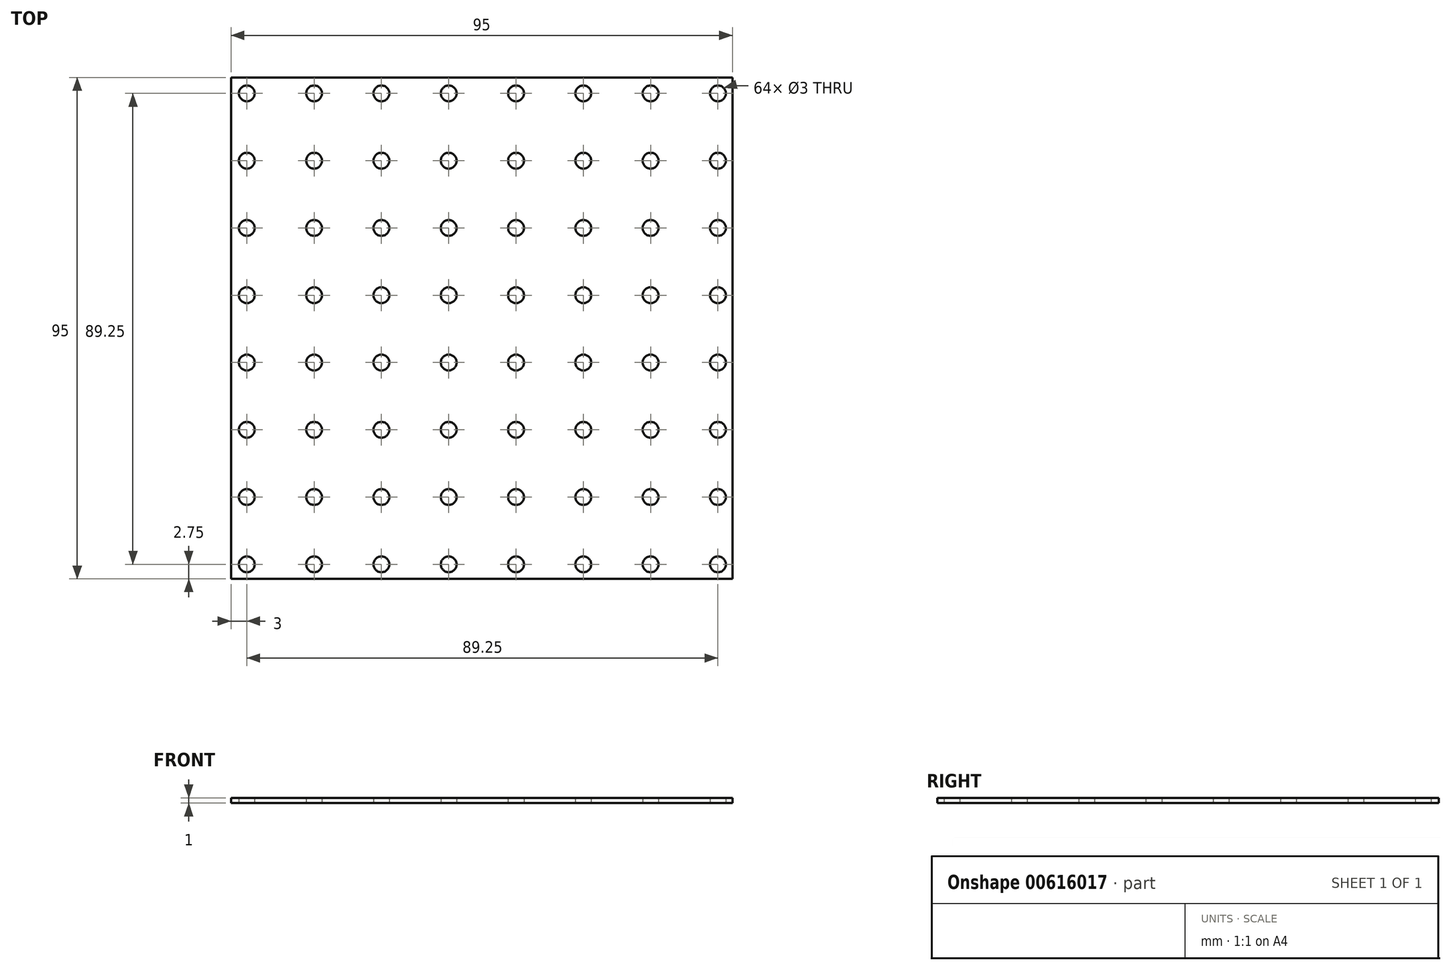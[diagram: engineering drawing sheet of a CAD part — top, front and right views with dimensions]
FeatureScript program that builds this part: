
annotation { "Feature Type Name" : "Feature", "Feature Type Description" : "" }
export const myFeature = defineFeature(function(context is Context, id is Id, definition is map)
    precondition{}
    {
        {
            var Q0;
            Q0=qCreatedBy(makeId("Top.planeOp"),FACE);
            var sketch = newSketch(context, id + "F0", { "sketchPlane" : qUnion([Q0])});
            skLineSegment(sketch, "E0.bottom", {"start": v(47.5, -47.5) * mm, "end": v(-47.5, -47.5) * mm});
            skLineSegment(sketch, "E0.top", {"start": v(47.5, 47.5) * mm, "end": v(-47.5, 47.5) * mm});
            skLineSegment(sketch, "E0.left", {"start": v(47.5, -47.5) * mm, "end": v(47.5, 47.5) * mm});
            skLineSegment(sketch, "E0.right", {"start": v(-47.5, -47.5) * mm, "end": v(-47.5, 47.5) * mm});
            skPoint(sketch, "E0.middle", {"position": v(0, 0) * mm});
            skCircle(sketch, "E1", {"center": v(-44.5, 44.5) * mm, "radius": 1.5 * mm});
            skCircle(sketch, "E2.0.1.0", {"center": v(-44.5, 31.75) * mm, "radius": 1.5 * mm});
            skCircle(sketch, "E2.0.2.0", {"center": v(-44.5, 19) * mm, "radius": 1.5 * mm});
            skCircle(sketch, "E2.0.3.0", {"center": v(-44.5, 6.25) * mm, "radius": 1.5 * mm});
            skCircle(sketch, "E2.0.4.0", {"center": v(-44.5, -6.5) * mm, "radius": 1.5 * mm});
            skCircle(sketch, "E2.0.5.0", {"center": v(-44.5, -19.25) * mm, "radius": 1.5 * mm});
            skCircle(sketch, "E2.0.6.0", {"center": v(-44.5, -32) * mm, "radius": 1.5 * mm});
            skCircle(sketch, "E2.0.7.0", {"center": v(-44.5, -44.75) * mm, "radius": 1.5 * mm});
            skCircle(sketch, "E2.1.0.0", {"center": v(-31.75, 44.5) * mm, "radius": 1.5 * mm});
            skCircle(sketch, "E2.1.1.0", {"center": v(-31.75, 31.75) * mm, "radius": 1.5 * mm});
            skCircle(sketch, "E2.1.2.0", {"center": v(-31.75, 19) * mm, "radius": 1.5 * mm});
            skCircle(sketch, "E2.1.3.0", {"center": v(-31.75, 6.25) * mm, "radius": 1.5 * mm});
            skCircle(sketch, "E2.1.4.0", {"center": v(-31.75, -6.5) * mm, "radius": 1.5 * mm});
            skCircle(sketch, "E2.1.5.0", {"center": v(-31.75, -19.25) * mm, "radius": 1.5 * mm});
            skCircle(sketch, "E2.1.6.0", {"center": v(-31.75, -32) * mm, "radius": 1.5 * mm});
            skCircle(sketch, "E2.1.7.0", {"center": v(-31.75, -44.75) * mm, "radius": 1.5 * mm});
            skCircle(sketch, "E2.2.0.0", {"center": v(-19, 44.5) * mm, "radius": 1.5 * mm});
            skCircle(sketch, "E2.2.1.0", {"center": v(-19, 31.75) * mm, "radius": 1.5 * mm});
            skCircle(sketch, "E2.2.2.0", {"center": v(-19, 19) * mm, "radius": 1.5 * mm});
            skCircle(sketch, "E2.2.3.0", {"center": v(-19, 6.25) * mm, "radius": 1.5 * mm});
            skCircle(sketch, "E2.2.4.0", {"center": v(-19, -6.5) * mm, "radius": 1.5 * mm});
            skCircle(sketch, "E2.2.5.0", {"center": v(-19, -19.25) * mm, "radius": 1.5 * mm});
            skCircle(sketch, "E2.2.6.0", {"center": v(-19, -32) * mm, "radius": 1.5 * mm});
            skCircle(sketch, "E2.2.7.0", {"center": v(-19, -44.75) * mm, "radius": 1.5 * mm});
            skCircle(sketch, "E2.3.0.0", {"center": v(-6.25, 44.5) * mm, "radius": 1.5 * mm});
            skCircle(sketch, "E2.3.1.0", {"center": v(-6.25, 31.75) * mm, "radius": 1.5 * mm});
            skCircle(sketch, "E2.3.2.0", {"center": v(-6.25, 19) * mm, "radius": 1.5 * mm});
            skCircle(sketch, "E2.3.3.0", {"center": v(-6.25, 6.25) * mm, "radius": 1.5 * mm});
            skCircle(sketch, "E2.3.4.0", {"center": v(-6.25, -6.5) * mm, "radius": 1.5 * mm});
            skCircle(sketch, "E2.3.5.0", {"center": v(-6.25, -19.25) * mm, "radius": 1.5 * mm});
            skCircle(sketch, "E2.3.6.0", {"center": v(-6.25, -32) * mm, "radius": 1.5 * mm});
            skCircle(sketch, "E2.3.7.0", {"center": v(-6.25, -44.75) * mm, "radius": 1.5 * mm});
            skCircle(sketch, "E2.4.0.0", {"center": v(6.5, 44.5) * mm, "radius": 1.5 * mm});
            skCircle(sketch, "E2.4.1.0", {"center": v(6.5, 31.75) * mm, "radius": 1.5 * mm});
            skCircle(sketch, "E2.4.2.0", {"center": v(6.5, 19) * mm, "radius": 1.5 * mm});
            skCircle(sketch, "E2.4.3.0", {"center": v(6.5, 6.25) * mm, "radius": 1.5 * mm});
            skCircle(sketch, "E2.4.4.0", {"center": v(6.5, -6.5) * mm, "radius": 1.5 * mm});
            skCircle(sketch, "E2.4.5.0", {"center": v(6.5, -19.25) * mm, "radius": 1.5 * mm});
            skCircle(sketch, "E2.4.6.0", {"center": v(6.5, -32) * mm, "radius": 1.5 * mm});
            skCircle(sketch, "E2.4.7.0", {"center": v(6.5, -44.75) * mm, "radius": 1.5 * mm});
            skCircle(sketch, "E2.5.0.0", {"center": v(19.25, 44.5) * mm, "radius": 1.5 * mm});
            skCircle(sketch, "E2.5.1.0", {"center": v(19.25, 31.75) * mm, "radius": 1.5 * mm});
            skCircle(sketch, "E2.5.2.0", {"center": v(19.25, 19) * mm, "radius": 1.5 * mm});
            skCircle(sketch, "E2.5.3.0", {"center": v(19.25, 6.25) * mm, "radius": 1.5 * mm});
            skCircle(sketch, "E2.5.4.0", {"center": v(19.25, -6.5) * mm, "radius": 1.5 * mm});
            skCircle(sketch, "E2.5.5.0", {"center": v(19.25, -19.25) * mm, "radius": 1.5 * mm});
            skCircle(sketch, "E2.5.6.0", {"center": v(19.25, -32) * mm, "radius": 1.5 * mm});
            skCircle(sketch, "E2.5.7.0", {"center": v(19.25, -44.75) * mm, "radius": 1.5 * mm});
            skCircle(sketch, "E2.6.0.0", {"center": v(32, 44.5) * mm, "radius": 1.5 * mm});
            skCircle(sketch, "E2.6.1.0", {"center": v(32, 31.75) * mm, "radius": 1.5 * mm});
            skCircle(sketch, "E2.6.2.0", {"center": v(32, 19) * mm, "radius": 1.5 * mm});
            skCircle(sketch, "E2.6.3.0", {"center": v(32, 6.25) * mm, "radius": 1.5 * mm});
            skCircle(sketch, "E2.6.4.0", {"center": v(32, -6.5) * mm, "radius": 1.5 * mm});
            skCircle(sketch, "E2.6.5.0", {"center": v(32, -19.25) * mm, "radius": 1.5 * mm});
            skCircle(sketch, "E2.6.6.0", {"center": v(32, -32) * mm, "radius": 1.5 * mm});
            skCircle(sketch, "E2.6.7.0", {"center": v(32, -44.75) * mm, "radius": 1.5 * mm});
            skCircle(sketch, "E2.7.0.0", {"center": v(44.75, 44.5) * mm, "radius": 1.5 * mm});
            skCircle(sketch, "E2.7.1.0", {"center": v(44.75, 31.75) * mm, "radius": 1.5 * mm});
            skCircle(sketch, "E2.7.2.0", {"center": v(44.75, 19) * mm, "radius": 1.5 * mm});
            skCircle(sketch, "E2.7.3.0", {"center": v(44.75, 6.25) * mm, "radius": 1.5 * mm});
            skCircle(sketch, "E2.7.4.0", {"center": v(44.75, -6.5) * mm, "radius": 1.5 * mm});
            skCircle(sketch, "E2.7.5.0", {"center": v(44.75, -19.25) * mm, "radius": 1.5 * mm});
            skCircle(sketch, "E2.7.6.0", {"center": v(44.75, -32) * mm, "radius": 1.5 * mm});
            skCircle(sketch, "E2.7.7.0", {"center": v(44.75, -44.75) * mm, "radius": 1.5 * mm});
            skLineSegment(sketch, "E2.direction1", {"start": v(-44.5, 44.5) * mm, "end": v(-31.75, 44.5) * mm, "construction": true});
            skLineSegment(sketch, "E2.direction2", {"start": v(-44.5, 44.5) * mm, "end": v(-44.5, 31.75) * mm, "construction": true});
            skSolve(sketch);
        }
        {
            var Q0;
            Q0=makeQuery(id+"F0.imprint","IMPRINT",FACE,{"disambiguationData":[TD([[makeQuery(id+"F0.imprint","IMPRINT",EDGE,{"derivedFrom":sQuery(id+"F0.wireOp",EDGE,"E0.bottom")}),-1.0]])]});
            extrude(context, id + "F1", {"entities" : qUnion([Q0]), "depth" : 1 * mm, "offsetDistance" : 25 * mm});
        }
    });
